# Revit family: Strong RF
name_source: partatom
category: Generic Models
units: mm (PartAtom-declared; Revit-internal decimal feet)

## family parameters
Always vertical = Yes
Can host rebar = No
Cut with Voids When Loaded = No
Host = Wall
Part Type = Normal
Room Calculation Point = No
Round Connector Dimension = Use Diameter
Shared = No

## types (18) — shared parameters
Manufacturer = Masterwatt B.V.
STG-W 351 = No
URL = https://masterwatt.nl
Voltage = 230 V
zero-valued in all types: Default Elevation

## per-type parameters (varying)
| type | Art. No. | Model | STG-B 1200 | STG-B 350 | STG-B 351 | STG-B 450 | STG-B 501 | STG-B 651 | STG-B 750 | STG-B 851 | STG-B 950 | STG-W 1200 | STG-W 350 | STG-W 450 | STG-W 501 | STG-W 651 | STG-W 750 | STG-W 851 | STG-W 950 | Watt |
| STG-W 351 RF | 880 111 350 | Infraroodpaneel STG-W 351 RF | No | No | No | No | No | No | No | No | No | No | No | No | No | No | No | No | No | 400 VA |
| STG-W 501 RF | 880 111 500 | Infraroodpaneel STG-W 501 RF | No | No | No | No | No | No | No | No | No | No | No | No | Yes | No | No | No | No | 500 VA |
| STG-W 651 RF | 880 111 650 | Infraroodpaneel STG-W 651 RF | No | No | No | No | No | No | No | No | No | No | No | No | No | Yes | No | No | No | 670 VA |
| STG-W 851 RF | 880 111 850 | Infraroodpaneel STG-W 851 RF | No | No | No | No | No | No | No | No | No | No | No | No | No | No | No | Yes | No | 820 VA |
| STG-W 350 RF | 880 101 350 | Infraroodpaneel STG-W 350 RF | No | No | No | No | No | No | No | No | No | No | Yes | No | No | No | No | No | No | 400 VA |
| STG-W 450 RF | 880 101 450 | Infraroodpaneel STG-W 450 RF | No | No | No | No | No | No | No | No | No | No | No | Yes | No | No | No | No | No | 500 VA |
| STG-W 750 RF | 880 101 750 | Infraroodpaneel STG-W 750 RF | No | No | No | No | No | No | No | No | No | No | No | No | No | No | Yes | No | No | 800 VA |
| STG-W 950 RF | 880 101 950 | Infraroodpaneel STG-W 950 RF | No | No | No | No | No | No | No | No | No | No | No | No | No | No | No | No | Yes | 1000 VA |
| STG-W 1200 RF | 880 101 120 | Infraroodpaneel STG-W 1200 RF | No | No | No | No | No | No | No | No | No | Yes | No | No | No | No | No | No | No | 1250 VA |
| STG-B 1200 RF | 880 101 121 | Infraroodpaneel STG-B 1200 RF | Yes | No | No | No | No | No | No | No | No | No | No | No | No | No | No | No | No | 1250 VA |
| STG-B 350 RF | 880 101 351 | Infraroodpaneel STG-B 350 RF | No | Yes | No | No | No | No | No | No | No | No | No | No | No | No | No | No | No | 400 VA |
| STG-B 351 RF | 880 111 351 | Infraroodpaneel STG-B 351 RF | No | No | Yes | No | No | No | No | No | No | No | No | No | No | No | No | No | No | 400 VA |
| STG-B 450 RF | 880 101 451 | Infraroodpaneel STG-B 450 RF | No | No | No | Yes | No | No | No | No | No | No | No | No | No | No | No | No | No | 500 VA |
| STG-B 501 RF | 880 111 501 | Infraroodpaneel STG-B 501 RF | No | No | No | No | Yes | No | No | No | No | No | No | No | No | No | No | No | No | 500 VA |
| STG-B- 651 RF | 880 111 651 | Infraroodpaneel STG-B 651 RF | No | No | No | No | No | Yes | No | No | No | No | No | No | No | No | No | No | No | 670 VA |
| STG-B 750 RF | 880 101 751 | Infraroodpaneel STG-B 750 RF | No | No | No | No | No | No | Yes | No | No | No | No | No | No | No | No | No | No | 800 VA |
| STG-B 851 RF | 880 111 851 | Infraroodpaneel STG-B 851 RF | No | No | No | No | No | No | No | Yes | No | No | No | No | No | No | No | No | No | 820 VA |
| STG-B 950 RF | 880 101 951 | Infraroodpaneel STG-B 950 RF | No | No | No | No | No | No | No | No | Yes | No | No | No | No | No | No | No | No | 1000 VA |

## geometry (parser evidence)
native form markers: Sweep x41
no freeform markers — native parametric forms only
